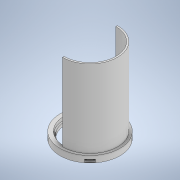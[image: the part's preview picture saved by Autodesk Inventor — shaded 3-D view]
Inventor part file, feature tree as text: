
AUTODESK INVENTOR PART (.ipt)
format: ipt  version: 2022 (Build 260153000, 153)  size: 163,840 bytes
history: native  units: mm
features: extrude x4, sketch x4
ambient origin geometry x8: Origin, YZ Plane, XZ Plane, XY Plane, X Axis, Y Axis, Z Axis, Center Point
bodies: Solid1 (feature_tree)
feature tree (8):
  extrude  "Extrusion1"  Depth=2.0mm
  extrude  "Extrusion2"  Depth=100.0mm TaperAngle=0.0deg
  extrude  "Extrusion3"  Depth=4.0mm
  extrude  "Extrusion6"  Depth=3.5mm
  sketch  "Sketch1"  dims[d0=64.0mm d1=2.0mm]
  sketch  "Sketch2"  dims[d2=2.0mm d3=100.0mm d4=0.0mm]
  sketch  "Sketch3"  dims[d5=4.0mm d6=0.0mm d7=74.0mm]
  sketch  "Sketch4"  dims[d8=8.0mm d9=0.0mm d10=11.0mm d11=45.0deg d16=24.0mm d17=40.0mm d19=360.0deg d21=3.5mm d22=0.0mm]
